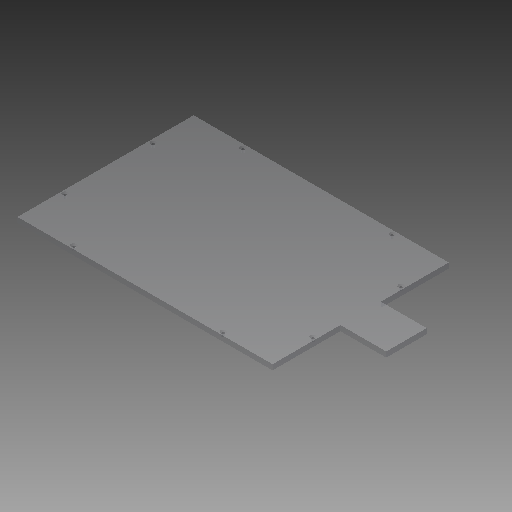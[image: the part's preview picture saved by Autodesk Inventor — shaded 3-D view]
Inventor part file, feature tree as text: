
AUTODESK INVENTOR PART (.ipt)
format: ipt  version: 2018 (Build 220112000, 112)  size: 113,152 bytes
history: native  units: mm
features: mirror x2, extrude x1, hole x1, sketch x1
ambient origin geometry x8: Origin, YZ Plane, XZ Plane, XY Plane, X Axis, Y Axis, Z Axis, Center Point
bodies: Volumenkörper1 (feature_tree)
feature tree (5):
  extrude  "Extrusion1"  Depth=289.5mm
  mirror  "Spiegeln1"
  hole  "Bohrung1"  [1 undecoded]
  mirror  "Spiegeln2"
  sketch  "Skizze1"  dims[d0=52.0mm d1=289.5mm d2=100.0mm d3=23.0mm d4=6.0mm d5=0.0mm d6=60.0mm d7=60.0mm d8=50.0mm d9=50.0mm d10=4.0mm d11=4.0mm d12=4.0mm d13=4.0mm d14=3.2mm d15=6.0mm d16=6.2mm d17=2.0mm d18=90.0deg d19=8.0mm d20=20.594885mm]
note: 1 required parameter value undecoded (feature->parameter linkage not recoverable at this tier; creation-order binding heuristic only, values carry confidence <= 0.55)
